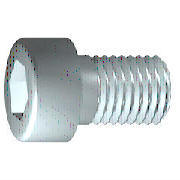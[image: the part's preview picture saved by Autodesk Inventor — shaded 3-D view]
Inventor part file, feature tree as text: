
AUTODESK INVENTOR PART (.ipt)
format: ipt  version: 2023.3 (Build 273359000, 359)  size: 201,216 bytes
history: native  units: mm (DEFAULTED — no unit token found)
features: sketch x2, other x1, extrude x1, plane x1, fillet x1
ambient origin geometry x7: Origin, YZ Plane, XY Plane, X Axis, Y Axis, Z Axis, Center Point
bodies: Solid1 (feature_tree)
feature tree (6):
  other  "Körper"
  extrude  "Loch"  Depth=1.4mm
  plane  "Work Plane1"
  fillet  "Fillet2"  Radius=1.4mm
  sketch  "Skizze1"  dims[d1=1.25mm d2=0.184135mm d3=1.4mm]
  sketch  "Skizze2"  dims[d4=0.6mm d5=60.0deg d6=1.4mm d7=1.4mm d8=1.501111mm d9=2.6mm d10=90.0deg d11=10.0mm d12=0.0mm d13=1.25mm d14=0.0mm d15=0.184035mm d16=0.184035mm d17=0.14mm d19=0.0mm d26=2.0mm d27=45.0deg d28=0.0mm d29=0.0mm d30=0.1mm]
